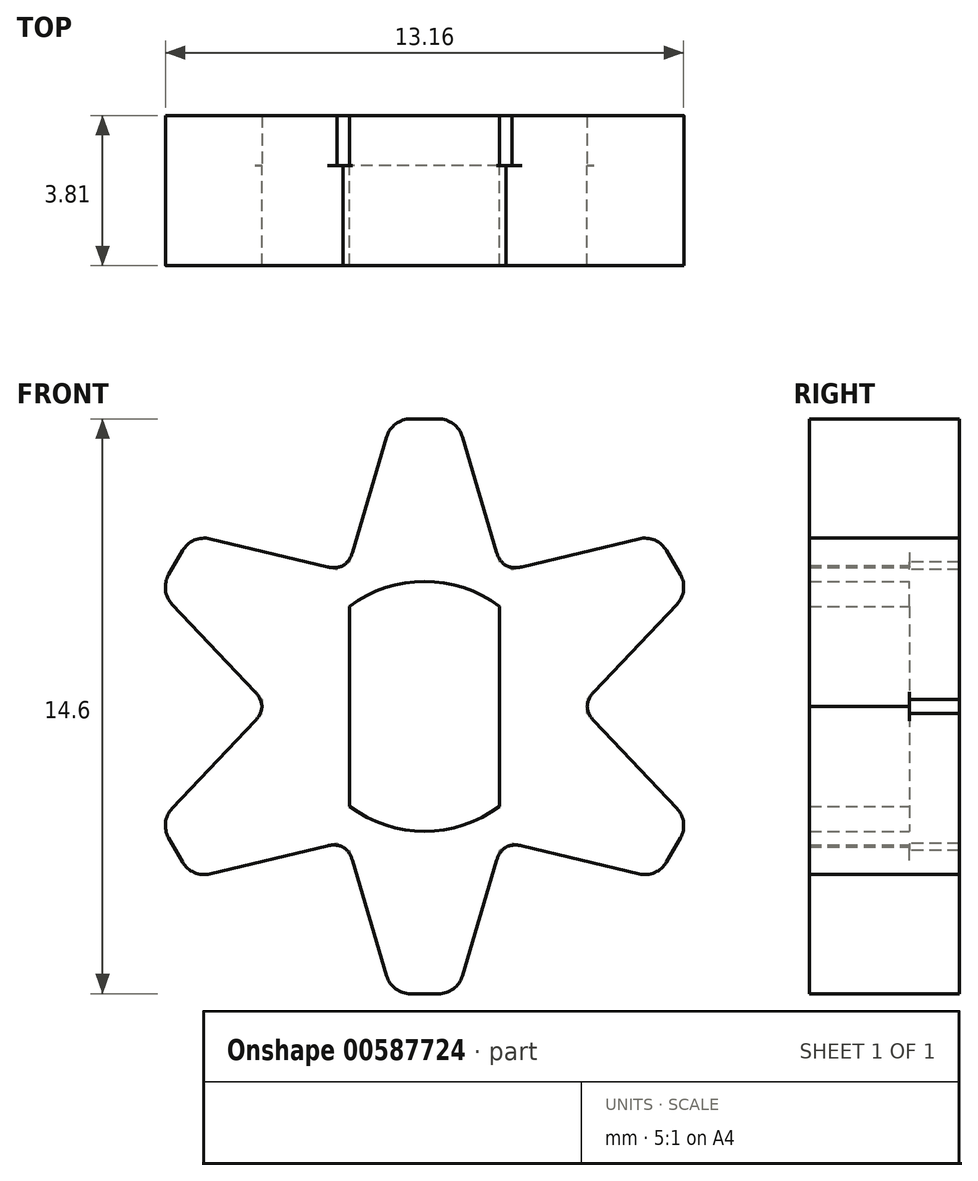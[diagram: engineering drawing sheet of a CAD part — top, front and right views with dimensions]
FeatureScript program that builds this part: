
annotation { "Feature Type Name" : "Feature", "Feature Type Description" : "" }
export const myFeature = defineFeature(function(context is Context, id is Id, definition is map)
    precondition{}
    {
        {
            var Q0;
            Q0=qCreatedBy(makeId("Front.planeOp"),FACE);
            var sketch = newSketch(context, id + "F0", { "sketchPlane" : qUnion([Q0])});
            skCircle(sketch, "E0", {"center": v(0, 0) * mm, "radius": 4.13 * mm});
            skLineSegment(sketch, "E1", {"start": v(-1.9, 3.66) * mm, "end": v(-0.96, 6.85) * mm});
            skLineSegment(sketch, "E2", {"start": v(-0.35, 7.3) * mm, "end": v(0.35, 7.3) * mm});
            skLineSegment(sketch, "E3", {"start": v(0.96, 6.85) * mm, "end": v(1.9, 3.66) * mm});
            skPoint(sketch, "E4.visualSharp", {"position": v(-0.83, 7.3) * mm});
            skArc(sketch, "E4.filletArc", {"start": v(-0.35, 7.3) * mm, "mid": v(-0.73, 7.18) * mm, "end": v(-0.96, 6.85) * mm});
            skPoint(sketch, "E5.visualSharp", {"position": v(0.83, 7.3) * mm});
            skArc(sketch, "E5.filletArc", {"start": v(0.96, 6.85) * mm, "mid": v(0.73, 7.18) * mm, "end": v(0.35, 7.3) * mm});
            skPoint(sketch, "E6", {"position": v(0, 4.13) * mm});
            skLineSegment(sketch, "E7.1.0", {"start": v(-5.45, 4.26) * mm, "end": v(-2.22, 3.48) * mm});
            skPoint(sketch, "E7.1.1", {"position": v(-3.57, 2.06) * mm});
            skLineSegment(sketch, "E7.1.2", {"start": v(-4.12, 0.18) * mm, "end": v(-6.41, 2.6) * mm});
            skLineSegment(sketch, "E7.1.3", {"start": v(-6.5, 3.35) * mm, "end": v(-6.15, 3.96) * mm});
            skArc(sketch, "E7.1.4", {"start": v(-6.5, 3.35) * mm, "mid": v(-6.58, 2.95) * mm, "end": v(-6.41, 2.6) * mm});
            skPoint(sketch, "E7.1.5", {"position": v(-6.74, 2.94) * mm});
            skPoint(sketch, "E7.1.6", {"position": v(-5.91, 4.37) * mm});
            skArc(sketch, "E7.1.7", {"start": v(-5.45, 4.26) * mm, "mid": v(-5.85, 4.22) * mm, "end": v(-6.15, 3.96) * mm});
            skLineSegment(sketch, "E7.2.0", {"start": v(-6.41, -2.6) * mm, "end": v(-4.12, -0.18) * mm});
            skPoint(sketch, "E7.2.1", {"position": v(-3.57, -2.06) * mm});
            skLineSegment(sketch, "E7.2.2", {"start": v(-2.22, -3.48) * mm, "end": v(-5.45, -4.26) * mm});
            skLineSegment(sketch, "E7.2.3", {"start": v(-6.15, -3.96) * mm, "end": v(-6.5, -3.35) * mm});
            skArc(sketch, "E7.2.4", {"start": v(-6.15, -3.96) * mm, "mid": v(-5.85, -4.22) * mm, "end": v(-5.45, -4.26) * mm});
            skPoint(sketch, "E7.2.5", {"position": v(-5.91, -4.37) * mm});
            skPoint(sketch, "E7.2.6", {"position": v(-6.74, -2.94) * mm});
            skArc(sketch, "E7.2.7", {"start": v(-6.41, -2.6) * mm, "mid": v(-6.58, -2.95) * mm, "end": v(-6.5, -3.35) * mm});
            skLineSegment(sketch, "E7.3.0", {"start": v(-0.96, -6.85) * mm, "end": v(-1.9, -3.66) * mm});
            skPoint(sketch, "E7.3.1", {"position": v(0, -4.13) * mm});
            skLineSegment(sketch, "E7.3.2", {"start": v(1.9, -3.66) * mm, "end": v(0.96, -6.85) * mm});
            skLineSegment(sketch, "E7.3.3", {"start": v(0.35, -7.3) * mm, "end": v(-0.35, -7.3) * mm});
            skArc(sketch, "E7.3.4", {"start": v(0.35, -7.3) * mm, "mid": v(0.73, -7.18) * mm, "end": v(0.96, -6.85) * mm});
            skPoint(sketch, "E7.3.5", {"position": v(0.83, -7.3) * mm});
            skPoint(sketch, "E7.3.6", {"position": v(-0.83, -7.3) * mm});
            skArc(sketch, "E7.3.7", {"start": v(-0.96, -6.85) * mm, "mid": v(-0.73, -7.18) * mm, "end": v(-0.35, -7.3) * mm});
            skCircle(sketch, "E8", {"center": v(0, 0) * mm, "radius": 8.45 * mm, "construction": true});
            skPoint(sketch, "E9.3.4.0", {"position": v(3.57, -2.06) * mm});
            skLineSegment(sketch, "E9.4.4.0", {"start": v(4.12, -0.18) * mm, "end": v(6.41, -2.6) * mm});
            skLineSegment(sketch, "E9.5.4.0", {"start": v(5.45, -4.26) * mm, "end": v(2.22, -3.48) * mm});
            skLineSegment(sketch, "E9.7.4.0", {"start": v(6.5, -3.35) * mm, "end": v(6.15, -3.96) * mm});
            skArc(sketch, "E9.10.4.0", {"start": v(6.5, -3.35) * mm, "mid": v(6.58, -2.95) * mm, "end": v(6.41, -2.6) * mm});
            skPoint(sketch, "E9.14.4.0", {"position": v(6.74, -2.94) * mm});
            skPoint(sketch, "E9.15.4.0", {"position": v(5.91, -4.37) * mm});
            skArc(sketch, "E9.16.4.0", {"start": v(5.45, -4.26) * mm, "mid": v(5.85, -4.22) * mm, "end": v(6.15, -3.96) * mm});
            skPoint(sketch, "E10.3.5.0", {"position": v(3.57, 2.06) * mm});
            skLineSegment(sketch, "E10.4.5.0", {"start": v(2.22, 3.48) * mm, "end": v(5.45, 4.26) * mm});
            skLineSegment(sketch, "E10.5.5.0", {"start": v(6.41, 2.6) * mm, "end": v(4.12, 0.18) * mm});
            skLineSegment(sketch, "E10.7.5.0", {"start": v(6.15, 3.96) * mm, "end": v(6.5, 3.35) * mm});
            skArc(sketch, "E10.10.5.0", {"start": v(6.15, 3.96) * mm, "mid": v(5.85, 4.22) * mm, "end": v(5.45, 4.26) * mm});
            skPoint(sketch, "E10.14.5.0", {"position": v(5.91, 4.37) * mm});
            skPoint(sketch, "E10.15.5.0", {"position": v(6.74, 2.94) * mm});
            skArc(sketch, "E10.16.5.0", {"start": v(6.41, 2.6) * mm, "mid": v(6.58, 2.95) * mm, "end": v(6.5, 3.35) * mm});
            skSolve(sketch);
        }
        {
            var Q0;
            Q0 = qSketchRegion(id + "F0", true);
            extrude(context, id + "F1", {"entities" : qUnion([Q0]), "depth" : 2.54 * mm, "offsetDistance" : 25.4 * mm});
        }
        {
            var Q0;
            Q0=makeQuery(id+"F1.opExtrude","SWEPT_EDGE",EDGE,{"disambiguationData":[OSD([sQuery(id+"F0.wireOp",EDGE,"E0"),sQuery(id+"F0.wireOp",EDGE,"E7.1.2")])]});
            var Q1;
            Q1=makeQuery(id+"F1.opExtrude","SWEPT_EDGE",EDGE,{"disambiguationData":[OSD([sQuery(id+"F0.wireOp",EDGE,"E0"),sQuery(id+"F0.wireOp",EDGE,"E7.2.0")])]});
            var Q2;
            Q2=makeQuery(id+"F1.opExtrude","SWEPT_EDGE",EDGE,{"disambiguationData":[OSD([sQuery(id+"F0.wireOp",EDGE,"E0"),sQuery(id+"F0.wireOp",EDGE,"E1")])]});
            var Q3;
            Q3=makeQuery(id+"F1.opExtrude","SWEPT_EDGE",EDGE,{"disambiguationData":[OSD([sQuery(id+"F0.wireOp",EDGE,"E0"),sQuery(id+"F0.wireOp",EDGE,"E7.9.2")])]});
            var Q4;
            Q4=makeQuery(id+"F1.opExtrude","SWEPT_EDGE",EDGE,{"disambiguationData":[OSD([sQuery(id+"F0.wireOp",EDGE,"E0"),sQuery(id+"F0.wireOp",EDGE,"E3")])]});
            var Q5;
            Q5=makeQuery(id+"F1.opExtrude","SWEPT_EDGE",EDGE,{"disambiguationData":[OSD([sQuery(id+"F0.wireOp",EDGE,"E0"),sQuery(id+"F0.wireOp",EDGE,"E7.1.0")])]});
            var Q6;
            Q6=makeQuery(id+"F1.opExtrude","SWEPT_EDGE",EDGE,{"disambiguationData":[OSD([sQuery(id+"F0.wireOp",EDGE,"E0"),sQuery(id+"F0.wireOp",EDGE,"E7.8.2")])]});
            var Q7;
            Q7=makeQuery(id+"F1.opExtrude","SWEPT_EDGE",EDGE,{"disambiguationData":[OSD([sQuery(id+"F0.wireOp",EDGE,"E0"),sQuery(id+"F0.wireOp",EDGE,"E7.9.0")])]});
            var Q8;
            Q8=makeQuery(id+"F1.opExtrude","SWEPT_EDGE",EDGE,{"disambiguationData":[OSD([sQuery(id+"F0.wireOp",EDGE,"E0"),sQuery(id+"F0.wireOp",EDGE,"E7.8.0")])]});
            var Q9;
            Q9=makeQuery(id+"F1.opExtrude","SWEPT_EDGE",EDGE,{"disambiguationData":[OSD([sQuery(id+"F0.wireOp",EDGE,"E0"),sQuery(id+"F0.wireOp",EDGE,"E7.7.2")])]});
            var Q10;
            Q10=makeQuery(id+"F1.opExtrude","SWEPT_EDGE",EDGE,{"disambiguationData":[OSD([sQuery(id+"F0.wireOp",EDGE,"E0"),sQuery(id+"F0.wireOp",EDGE,"E7.6.2")])]});
            var Q11;
            Q11=makeQuery(id+"F1.opExtrude","SWEPT_EDGE",EDGE,{"disambiguationData":[OSD([sQuery(id+"F0.wireOp",EDGE,"E0"),sQuery(id+"F0.wireOp",EDGE,"E7.7.0")])]});
            var Q12;
            Q12=makeQuery(id+"F1.opExtrude","SWEPT_EDGE",EDGE,{"disambiguationData":[OSD([sQuery(id+"F0.wireOp",EDGE,"E0"),sQuery(id+"F0.wireOp",EDGE,"E7.5.2")])]});
            var Q13;
            Q13=makeQuery(id+"F1.opExtrude","SWEPT_EDGE",EDGE,{"disambiguationData":[OSD([sQuery(id+"F0.wireOp",EDGE,"E0"),sQuery(id+"F0.wireOp",EDGE,"E7.6.0")])]});
            var Q14;
            Q14=makeQuery(id+"F1.opExtrude","SWEPT_EDGE",EDGE,{"disambiguationData":[OSD([sQuery(id+"F0.wireOp",EDGE,"E0"),sQuery(id+"F0.wireOp",EDGE,"E7.5.0")])]});
            var Q15;
            Q15=makeQuery(id+"F1.opExtrude","SWEPT_EDGE",EDGE,{"disambiguationData":[OSD([sQuery(id+"F0.wireOp",EDGE,"E0"),sQuery(id+"F0.wireOp",EDGE,"E7.4.2")])]});
            var Q16;
            Q16=makeQuery(id+"F1.opExtrude","SWEPT_EDGE",EDGE,{"disambiguationData":[OSD([sQuery(id+"F0.wireOp",EDGE,"E0"),sQuery(id+"F0.wireOp",EDGE,"E7.4.0")])]});
            var Q17;
            Q17=makeQuery(id+"F1.opExtrude","SWEPT_EDGE",EDGE,{"disambiguationData":[OSD([sQuery(id+"F0.wireOp",EDGE,"E0"),sQuery(id+"F0.wireOp",EDGE,"E7.3.2")])]});
            var Q18;
            Q18=makeQuery(id+"F1.opExtrude","SWEPT_EDGE",EDGE,{"disambiguationData":[OSD([sQuery(id+"F0.wireOp",EDGE,"E0"),sQuery(id+"F0.wireOp",EDGE,"E7.2.2")])]});
            var Q19;
            Q19=makeQuery(id+"F1.opExtrude","SWEPT_EDGE",EDGE,{"disambiguationData":[OSD([sQuery(id+"F0.wireOp",EDGE,"E0"),sQuery(id+"F0.wireOp",EDGE,"E7.3.0")])]});
            fillet(context, id + "F2", {"entities" : qUnion([Q0, Q1, Q2, Q3, Q4, Q5, Q6, Q7, Q8, Q9, Q10, Q11, Q12, Q13, Q14, Q15, Q16, Q17, Q18, Q19]), "radius" : 0.64 * mm, "tangentPropagation" : true, "allowEdgeOverflow" : false});
        }
        {
            var Q0;
            Q0=makeQuery(id+"F1.opExtrude","CAP_FACE",FACE,{"disambiguationData":[OSD([sQuery(id+"F0.wireOp",EDGE,"E0"),sQuery(id+"F0.wireOp",EDGE,"E1"),sQuery(id+"F0.wireOp",EDGE,"E2"),sQuery(id+"F0.wireOp",EDGE,"E3"),sQuery(id+"F0.wireOp",EDGE,"E4.filletArc"),sQuery(id+"F0.wireOp",EDGE,"E5.filletArc"),sQuery(id+"F0.wireOp",EDGE,"E7.1.0"),sQuery(id+"F0.wireOp",EDGE,"E7.1.2"),sQuery(id+"F0.wireOp",EDGE,"E7.1.3"),sQuery(id+"F0.wireOp",EDGE,"E7.1.4"),sQuery(id+"F0.wireOp",EDGE,"E7.1.7"),sQuery(id+"F0.wireOp",EDGE,"E7.2.0"),sQuery(id+"F0.wireOp",EDGE,"E7.2.2"),sQuery(id+"F0.wireOp",EDGE,"E7.2.3"),sQuery(id+"F0.wireOp",EDGE,"E7.2.4"),sQuery(id+"F0.wireOp",EDGE,"E7.2.7"),sQuery(id+"F0.wireOp",EDGE,"E7.3.0"),sQuery(id+"F0.wireOp",EDGE,"E7.3.2"),sQuery(id+"F0.wireOp",EDGE,"E7.3.3"),sQuery(id+"F0.wireOp",EDGE,"E7.3.4"),sQuery(id+"F0.wireOp",EDGE,"E7.3.7"),sQuery(id+"F0.wireOp",EDGE,"E7.4.0"),sQuery(id+"F0.wireOp",EDGE,"E7.4.2"),sQuery(id+"F0.wireOp",EDGE,"E7.4.3"),sQuery(id+"F0.wireOp",EDGE,"E7.4.4"),sQuery(id+"F0.wireOp",EDGE,"E7.4.7"),sQuery(id+"F0.wireOp",EDGE,"E7.5.0"),sQuery(id+"F0.wireOp",EDGE,"E7.5.2"),sQuery(id+"F0.wireOp",EDGE,"E7.5.3"),sQuery(id+"F0.wireOp",EDGE,"E7.5.4"),sQuery(id+"F0.wireOp",EDGE,"E7.5.7"),sQuery(id+"F0.wireOp",EDGE,"E7.6.0"),sQuery(id+"F0.wireOp",EDGE,"E7.6.2"),sQuery(id+"F0.wireOp",EDGE,"E7.6.3"),sQuery(id+"F0.wireOp",EDGE,"E7.6.4"),sQuery(id+"F0.wireOp",EDGE,"E7.6.7"),sQuery(id+"F0.wireOp",EDGE,"E7.7.0"),sQuery(id+"F0.wireOp",EDGE,"E7.7.2"),sQuery(id+"F0.wireOp",EDGE,"E7.7.3"),sQuery(id+"F0.wireOp",EDGE,"E7.7.4"),sQuery(id+"F0.wireOp",EDGE,"E7.7.7"),sQuery(id+"F0.wireOp",EDGE,"E7.8.0"),sQuery(id+"F0.wireOp",EDGE,"E7.8.2"),sQuery(id+"F0.wireOp",EDGE,"E7.8.3"),sQuery(id+"F0.wireOp",EDGE,"E7.8.4"),sQuery(id+"F0.wireOp",EDGE,"E7.8.7"),sQuery(id+"F0.wireOp",EDGE,"E7.9.0"),sQuery(id+"F0.wireOp",EDGE,"E7.9.2"),sQuery(id+"F0.wireOp",EDGE,"E7.9.3"),sQuery(id+"F0.wireOp",EDGE,"E7.9.4"),sQuery(id+"F0.wireOp",EDGE,"E7.9.7")])],"isStart":true});
            var sketch = newSketch(context, id + "F3", { "sketchPlane" : qUnion([Q0])});
            skArc(sketch, "E11", {"start": v(-1.9, -2.54) * mm, "mid": v(0, -3.18) * mm, "end": v(1.9, -2.54) * mm});
            skLineSegment(sketch, "E12", {"start": v(-1.9, 2.54) * mm, "end": v(-1.9, -2.54) * mm});
            skLineSegment(sketch, "E13", {"start": v(1.9, 2.54) * mm, "end": v(1.9, -2.54) * mm});
            skArc(sketch, "E14.trimOffspring", {"start": v(1.9, 2.54) * mm, "mid": v(0, 3.18) * mm, "end": v(-1.9, 2.54) * mm});
            skSolve(sketch);
        }
        {
            var Q0;
            Q0 = qSketchRegion(id + "F3", true);
            extrude(context, id + "F4", {"entities" : qUnion([Q0]), "operationType" : NewBodyOperationType.REMOVE, "oppositeDirection" : true, "depth" : 25.4 * mm, "offsetDistance" : 25.4 * mm});
        }
        {
            var Q0;
            Q0 = qSketchRegion(id + "F0", true);
            extrude(context, id + "F5", {"entities" : qUnion([Q0]), "operationType" : NewBodyOperationType.ADD, "oppositeDirection" : true, "depth" : 1.27 * mm, "offsetDistance" : 25.4 * mm});
        }
    });
